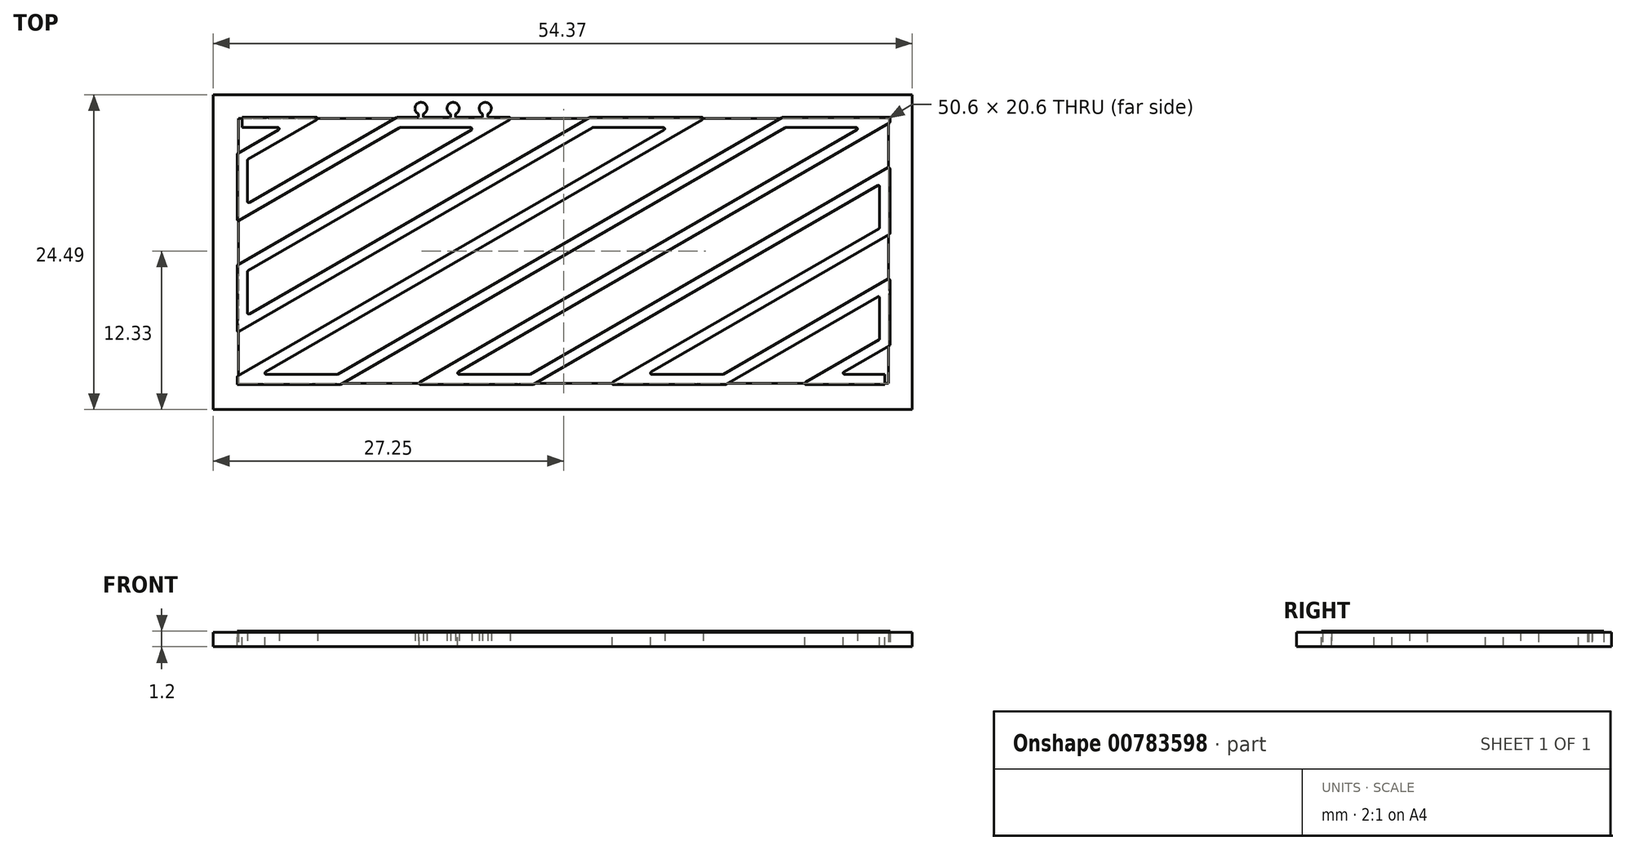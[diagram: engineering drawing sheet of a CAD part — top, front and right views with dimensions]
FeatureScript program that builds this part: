
annotation { "Feature Type Name" : "Feature", "Feature Type Description" : "" }
export const myFeature = defineFeature(function(context is Context, id is Id, definition is map)
    precondition{}
    {
        {
            var Q0;
            Q0=qCreatedBy(makeId("Top.planeOp"),FACE);
            var sketch = newSketch(context, id + "F0", { "sketchPlane" : qUnion([Q0])});
            skLineSegment(sketch, "E0.bottom", {"start": v(0, 0) * mm, "end": v(50, 0) * mm});
            skLineSegment(sketch, "E0.top", {"start": v(0, 20) * mm, "end": v(50, 20) * mm});
            skLineSegment(sketch, "E0.left", {"start": v(0, 0) * mm, "end": v(0, 20) * mm});
            skLineSegment(sketch, "E0.right", {"start": v(50, 0) * mm, "end": v(50, 20) * mm});
            skSolve(sketch);
        }
        {
            var Q0;
            Q0=qCreatedBy(makeId("Top.planeOp"),FACE);
            var sketch = newSketch(context, id + "F1", { "sketchPlane" : qUnion([Q0])});
            skLineSegment(sketch, "E1", {"start": v(0, 0) * mm, "end": v(34.64, 20) * mm});
            skLineSegment(sketch, "E2.1.0.0", {"start": v(7.5, 0) * mm, "end": v(42.14, 20) * mm});
            skLineSegment(sketch, "E2.2.0.0", {"start": v(15, 0) * mm, "end": v(49.64, 20) * mm});
            skLineSegment(sketch, "E2.3.0.0", {"start": v(22.5, 0) * mm, "end": v(50, 15.88) * mm});
            skLineSegment(sketch, "E2.4.0.0", {"start": v(30, 0) * mm, "end": v(50, 11.55) * mm});
            skLineSegment(sketch, "E2.5.0.0", {"start": v(37.5, 0) * mm, "end": v(50, 7.22) * mm});
            skLineSegment(sketch, "E2.6.0.0", {"start": v(45, 0) * mm, "end": v(50, 2.89) * mm});
            skLineSegment(sketch, "E3.1.0.0", {"start": v(0, 4.33) * mm, "end": v(27.14, 20) * mm});
            skLineSegment(sketch, "E3.2.0.0", {"start": v(0, 8.66) * mm, "end": v(19.64, 20) * mm});
            skLineSegment(sketch, "E3.3.0.0", {"start": v(0, 13) * mm, "end": v(12.14, 20) * mm});
            skLineSegment(sketch, "E3.4.0.0", {"start": v(0, 17.32) * mm, "end": v(4.64, 20) * mm});
            skLineSegment(sketch, "E4", {"start": v(0, 0) * mm, "end": v(7.5, 0) * mm});
            skLineSegment(sketch, "E5.1.0.0", {"start": v(15, 0) * mm, "end": v(22.5, 0) * mm});
            skLineSegment(sketch, "E5.2.0.0", {"start": v(30, 0) * mm, "end": v(37.5, 0) * mm});
            skLineSegment(sketch, "E5.3.0.0", {"start": v(45, 0) * mm, "end": v(50, 0) * mm});
            skLineSegment(sketch, "E6", {"start": v(0, 20) * mm, "end": v(4.64, 20) * mm});
            skLineSegment(sketch, "E7.1.0.0", {"start": v(12.14, 20) * mm, "end": v(19.64, 20) * mm});
            skLineSegment(sketch, "E7.2.0.0", {"start": v(27.14, 20) * mm, "end": v(34.64, 20) * mm});
            skLineSegment(sketch, "E7.3.0.0", {"start": v(42.14, 20) * mm, "end": v(49.64, 20) * mm});
            skPoint(sketch, "E8.orphan", {"position": v(-2.86, 20) * mm});
            skPoint(sketch, "E9.orphan", {"position": v(52.5, 0) * mm});
            skLineSegment(sketch, "E10", {"start": v(0, 4.33) * mm, "end": v(0, 8.66) * mm});
            skLineSegment(sketch, "E11", {"start": v(0, 13) * mm, "end": v(0, 17.32) * mm});
            skLineSegment(sketch, "E12", {"start": v(50, 15.88) * mm, "end": v(50, 11.55) * mm});
            skLineSegment(sketch, "E13", {"start": v(50, 7.22) * mm, "end": v(50, 2.89) * mm});
            skSolve(sketch);
        }
        {
            var Q0;
            Q0=sQuery(id+"F1.wireOp",VERTEX,"E6.start");
            var Q1;
            Q1=sQuery(id+"F1.wireOp",EDGE,"E6");
            cPlane(context, id + "F2", {"entities" : qUnion([Q0, Q1]), "cplaneType" : CPlaneType.LINE_POINT, "offset" : 25 * mm, "width" : 150 * mm, "height" : 150 * mm});
        }
        {
            var Q0;
            Q0=qCreatedBy(id+"F2.planeOp",FACE);
            var sketch = newSketch(context, id + "F3", { "sketchPlane" : qUnion([Q0])});
            skPoint(sketch, "E14.0", {"position": v(20, 0) * mm});
            skLineSegment(sketch, "E15", {"start": v(20, 0) * mm, "end": v(20.4, 0) * mm});
            skLineSegment(sketch, "E16", {"start": v(20.4, 0) * mm, "end": v(20.4, 1.2) * mm});
            skLineSegment(sketch, "E17", {"start": v(20.4, 1.2) * mm, "end": v(20, 1.2) * mm});
            skLineSegment(sketch, "E18", {"start": v(20, -0.76) * mm, "end": v(20, 2.5) * mm, "construction": true});
            skLineSegment(sketch, "E19.MirrorCS", {"start": v(19.6, 1.2) * mm, "end": v(20, 1.2) * mm});
            skLineSegment(sketch, "E20.MirrorCS", {"start": v(20, 0) * mm, "end": v(19.6, 0) * mm});
            skLineSegment(sketch, "E21.MirrorCS", {"start": v(19.6, 0) * mm, "end": v(19.6, 1.2) * mm});
            skSolve(sketch);
        }
        {
            var Q0;
            Q0=qSketchRegion(id+"F3",true);
            var Q1;
            Q1=sQuery(id+"F1.wireOp",EDGE,"E6");
            var Q2;
            Q2=sQuery(id+"F1.wireOp",EDGE,"E3.4.0.0");
            var Q3;
            Q3=sQuery(id+"F1.wireOp",EDGE,"E11");
            var Q4;
            Q4=sQuery(id+"F1.wireOp",EDGE,"E3.3.0.0");
            var Q5;
            Q5=sQuery(id+"F1.wireOp",EDGE,"E7.1.0.0");
            var Q6;
            Q6=sQuery(id+"F1.wireOp",EDGE,"E3.2.0.0");
            var Q7;
            Q7=sQuery(id+"F1.wireOp",EDGE,"E10");
            var Q8;
            Q8=sQuery(id+"F1.wireOp",EDGE,"E3.1.0.0");
            var Q9;
            Q9=sQuery(id+"F1.wireOp",EDGE,"E7.2.0.0");
            var Q10;
            Q10=sQuery(id+"F1.wireOp",EDGE,"E1");
            var Q11;
            Q11=sQuery(id+"F1.wireOp",EDGE,"E4");
            var Q12;
            Q12=sQuery(id+"F1.wireOp",EDGE,"E2.1.0.0");
            var Q13;
            Q13=sQuery(id+"F1.wireOp",EDGE,"E2.2.0.0");
            var Q14;
            Q14=sQuery(id+"F1.wireOp",EDGE,"E7.3.0.0");
            var Q15;
            Q15=sQuery(id+"F1.wireOp",EDGE,"E5.1.0.0");
            var Q16;
            Q16=sQuery(id+"F1.wireOp",EDGE,"E2.3.0.0");
            var Q17;
            Q17=sQuery(id+"F1.wireOp",EDGE,"E12");
            var Q18;
            Q18=sQuery(id+"F1.wireOp",EDGE,"E2.4.0.0");
            var Q19;
            Q19=sQuery(id+"F1.wireOp",EDGE,"E5.2.0.0");
            var Q20;
            Q20=sQuery(id+"F1.wireOp",EDGE,"E2.5.0.0");
            var Q21;
            Q21=sQuery(id+"F1.wireOp",EDGE,"E13");
            var Q22;
            Q22=sQuery(id+"F1.wireOp",EDGE,"E2.6.0.0");
            var Q23;
            Q23=sQuery(id+"F1.wireOp",EDGE,"E5.3.0.0");
            sweep(context, id + "F4", {"profiles" : qUnion([Q0]), "path" : qUnion([Q1, Q2, Q3, Q4, Q5, Q6, Q7, Q8, Q9, Q10, Q11, Q12, Q13, Q14, Q15, Q16, Q17, Q18, Q19, Q20, Q21, Q22, Q23])});
        }
        {
            var Q0;
            Q0=qCreatedBy(makeId("Top.planeOp"),FACE);
            var sketch = newSketch(context, id + "F5", { "sketchPlane" : qUnion([Q0])});
            skLineSegment(sketch, "E22.0", {"start": v(-0.4, 8.9) * mm, "end": v(-0.4, 3.64) * mm});
            skLineSegment(sketch, "E23.0", {"start": v(0, 20.4) * mm, "end": v(6.13, 20.4) * mm});
            skLineSegment(sketch, "E24.0", {"start": v(28.5, -0.4) * mm, "end": v(37.6, -0.4) * mm});
            skLineSegment(sketch, "E25.0", {"start": v(50.4, 16.57) * mm, "end": v(50.4, 11.32) * mm});
            skLineSegment(sketch, "E26.bottom", {"start": v(-0.4, 20.4) * mm, "end": v(50.4, 20.4) * mm});
            skLineSegment(sketch, "E26.top", {"start": v(-0.4, -0.4) * mm, "end": v(50.4, -0.4) * mm});
            skLineSegment(sketch, "E26.left", {"start": v(-0.4, 20.4) * mm, "end": v(-0.4, -0.4) * mm});
            skLineSegment(sketch, "E26.right", {"start": v(50.4, 20.4) * mm, "end": v(50.4, -0.4) * mm});
            skLineSegment(sketch, "E27.bottom", {"start": v(-6.4, 28.18) * mm, "end": v(56.43, 28.18) * mm});
            skLineSegment(sketch, "E27.top", {"start": v(-6.4, -9.1) * mm, "end": v(56.43, -9.1) * mm});
            skLineSegment(sketch, "E27.left", {"start": v(-6.4, 28.18) * mm, "end": v(-6.4, -9.1) * mm});
            skLineSegment(sketch, "E27.right", {"start": v(56.43, 28.18) * mm, "end": v(56.43, -9.1) * mm});
            skSolve(sketch);
        }
        {
            var Q0;
            {var subQ1=sQuery(id+"F5.wireOp",EDGE,"E22.0");Q0=makeQuery(id+"F5.imprint","IMPRINT",FACE,{"disambiguationData":[TD([[makeQuery(id+"F5.imprint","IMPRINT",EDGE,{"derivedFrom":subQ1}),-1.0]])]});}
            extrude(context, id + "F6", {"entities" : qUnion([Q0]), "depth" : 25 * mm, "offsetDistance" : 25 * mm});
        }
        {
            var Q0;
            Q0=makeQuery(id+"F6.opExtrude","SWEPT_BODY",BODY,{"disambiguationData":[OSD([sQuery(id+"F5.wireOp",EDGE,"E22.0"),sQuery(id+"F5.wireOp",EDGE,"E23.0"),sQuery(id+"F5.wireOp",EDGE,"E24.0"),sQuery(id+"F5.wireOp",EDGE,"E25.0"),sQuery(id+"F5.wireOp",EDGE,"E26.bottom"),sQuery(id+"F5.wireOp",EDGE,"E26.top"),sQuery(id+"F5.wireOp",EDGE,"E26.left"),sQuery(id+"F5.wireOp",EDGE,"E26.right"),sQuery(id+"F5.wireOp",EDGE,"E27.bottom"),sQuery(id+"F5.wireOp",EDGE,"E27.top"),sQuery(id+"F5.wireOp",EDGE,"E27.left"),sQuery(id+"F5.wireOp",EDGE,"E27.right")])]});
            var Q1;
            Q1=makeQuery(id+"F4.opSweep","SWEPT_BODY",BODY,{"disambiguationData":[OSD([sQuery(id+"F1.wireOp",EDGE,"E2.1.0.0"),sQuery(id+"F3.wireOp",EDGE,"E15"),sQuery(id+"F3.wireOp",EDGE,"E16"),sQuery(id+"F3.wireOp",EDGE,"E17"),sQuery(id+"F3.wireOp",EDGE,"E19.MirrorCS"),sQuery(id+"F3.wireOp",EDGE,"E20.MirrorCS"),sQuery(id+"F3.wireOp",EDGE,"E21.MirrorCS")])]});
            booleanBodies(context, id + "F7", {"operationType" : BooleanOperationType.SUBTRACTION, "tools" : qUnion([Q0]), "targets" : qUnion([Q1])});
        }
        {
            var Q0;
            Q0=qCreatedBy(makeId("Top.planeOp"),FACE);
            var sketch = newSketch(context, id + "F8", { "sketchPlane" : qUnion([Q0])});
            skLineSegment(sketch, "E28.0", {"start": v(-0.3, 20.3) * mm, "end": v(50.3, 20.3) * mm});
            skLineSegment(sketch, "E28.1", {"start": v(-0.3, 20.3) * mm, "end": v(-0.3, -0.3) * mm});
            skLineSegment(sketch, "E28.2", {"start": v(-0.3, -0.3) * mm, "end": v(50.3, -0.3) * mm});
            skLineSegment(sketch, "E28.3", {"start": v(50.3, 20.3) * mm, "end": v(50.3, -0.3) * mm});
            skSolve(sketch);
        }
        {
            var Q0;
            Q0=qSketchRegion(id+"F8",true);
            extrude(context, id + "F9", {"entities" : qUnion([Q0]), "depth" : 1.1 * mm, "offsetDistance" : 25 * mm});
        }
        {
            var Q0;
            Q0=makeQuery(id+"F4.opSweep","MID_CAP_EDGE",EDGE,{"disambiguationData":[OSD([sQuery(id+"F1.wireOp",VERTEX,"E11.end"),sQuery(id+"F3.wireOp",EDGE,"E21.MirrorCS")])],"capPos":2.0});
            var Q1;
            Q1=makeQuery(id+"F4.opSweep","MID_CAP_EDGE",EDGE,{"disambiguationData":[OSD([sQuery(id+"F1.wireOp",VERTEX,"E3.4.0.0.end"),sQuery(id+"F3.wireOp",EDGE,"E21.MirrorCS")])],"capPos":1.0});
            var Q2;
            Q2=makeQuery(id+"F4.opSweep","MID_CAP_EDGE",EDGE,{"disambiguationData":[OSD([sQuery(id+"F1.wireOp",VERTEX,"E3.4.0.0.end"),sQuery(id+"F3.wireOp",EDGE,"E16")])],"capPos":1.0});
            var Q3;
            Q3=makeQuery(id+"F4.opSweep","MID_CAP_EDGE",EDGE,{"disambiguationData":[OSD([sQuery(id+"F1.wireOp",VERTEX,"E11.end"),sQuery(id+"F3.wireOp",EDGE,"E16")])],"capPos":2.0});
            var Q4;
            Q4=makeQuery(id+"F4.opSweep","MID_CAP_EDGE",EDGE,{"disambiguationData":[OSD([sQuery(id+"F1.wireOp",VERTEX,"E3.3.0.0.start"),sQuery(id+"F3.wireOp",EDGE,"E16")])],"capPos":3.0});
            var Q5;
            Q5=makeQuery(id+"F4.opSweep","MID_CAP_EDGE",EDGE,{"disambiguationData":[OSD([sQuery(id+"F1.wireOp",VERTEX,"E3.3.0.0.start"),sQuery(id+"F3.wireOp",EDGE,"E21.MirrorCS")])],"capPos":3.0});
            var Q6;
            Q6=makeQuery(id+"F4.opSweep","MID_CAP_EDGE",EDGE,{"disambiguationData":[OSD([sQuery(id+"F1.wireOp",VERTEX,"E7.1.0.0.start"),sQuery(id+"F3.wireOp",EDGE,"E21.MirrorCS")])],"capPos":4.0});
            var Q7;
            Q7=makeQuery(id+"F4.opSweep","MID_CAP_EDGE",EDGE,{"disambiguationData":[OSD([sQuery(id+"F1.wireOp",VERTEX,"E7.1.0.0.start"),sQuery(id+"F3.wireOp",EDGE,"E16")])],"capPos":4.0});
            var Q8;
            Q8=makeQuery(id+"F4.opSweep","MID_CAP_EDGE",EDGE,{"disambiguationData":[OSD([sQuery(id+"F1.wireOp",VERTEX,"E3.2.0.0.end"),sQuery(id+"F3.wireOp",EDGE,"E21.MirrorCS")])],"capPos":5.0});
            var Q9;
            Q9=makeQuery(id+"F4.opSweep","MID_CAP_EDGE",EDGE,{"disambiguationData":[OSD([sQuery(id+"F1.wireOp",VERTEX,"E3.2.0.0.end"),sQuery(id+"F3.wireOp",EDGE,"E16")])],"capPos":5.0});
            var Q10;
            Q10=makeQuery(id+"F4.opSweep","MID_CAP_EDGE",EDGE,{"disambiguationData":[OSD([sQuery(id+"F1.wireOp",VERTEX,"E7.2.0.0.start"),sQuery(id+"F3.wireOp",EDGE,"E16")])],"capPos":8.0});
            var Q11;
            Q11=makeQuery(id+"F4.opSweep","MID_CAP_EDGE",EDGE,{"disambiguationData":[OSD([sQuery(id+"F1.wireOp",VERTEX,"E10.end"),sQuery(id+"F3.wireOp",EDGE,"E21.MirrorCS")])],"capPos":6.0});
            var Q12;
            Q12=makeQuery(id+"F4.opSweep","MID_CAP_EDGE",EDGE,{"disambiguationData":[OSD([sQuery(id+"F1.wireOp",VERTEX,"E10.end"),sQuery(id+"F3.wireOp",EDGE,"E16")])],"capPos":6.0});
            var Q13;
            Q13=makeQuery(id+"F4.opSweep","MID_CAP_EDGE",EDGE,{"disambiguationData":[OSD([sQuery(id+"F1.wireOp",VERTEX,"E3.1.0.0.start"),sQuery(id+"F3.wireOp",EDGE,"E16")])],"capPos":7.0});
            var Q14;
            Q14=makeQuery(id+"F4.opSweep","MID_CAP_EDGE",EDGE,{"disambiguationData":[OSD([sQuery(id+"F1.wireOp",VERTEX,"E3.1.0.0.start"),sQuery(id+"F3.wireOp",EDGE,"E21.MirrorCS")])],"capPos":7.0});
            var Q15;
            Q15=makeQuery(id+"F4.opSweep","MID_CAP_EDGE",EDGE,{"disambiguationData":[OSD([sQuery(id+"F1.wireOp",VERTEX,"E7.2.0.0.start"),sQuery(id+"F3.wireOp",EDGE,"E21.MirrorCS")])],"capPos":8.0});
            var Q16;
            Q16=makeQuery(id+"F4.opSweep","MID_CAP_EDGE",EDGE,{"disambiguationData":[OSD([sQuery(id+"F1.wireOp",VERTEX,"E1.end"),sQuery(id+"F3.wireOp",EDGE,"E21.MirrorCS")])],"capPos":9.0});
            var Q17;
            Q17=makeQuery(id+"F4.opSweep","MID_CAP_EDGE",EDGE,{"disambiguationData":[OSD([sQuery(id+"F1.wireOp",VERTEX,"E1.end"),sQuery(id+"F3.wireOp",EDGE,"E16")])],"capPos":9.0});
            var Q18;
            Q18=makeQuery(id+"F4.opSweep","MID_CAP_EDGE",EDGE,{"disambiguationData":[OSD([sQuery(id+"F1.wireOp",VERTEX,"E7.3.0.0.start"),sQuery(id+"F3.wireOp",EDGE,"E16")])],"capPos":12.0});
            var Q19;
            Q19=makeQuery(id+"F7.opBoolean","INTERSECT",EDGE,{"derivedFrom":[makeQuery(id+"F4.opSweep","SWEPT_FACE",FACE,{"disambiguationData":[OSD([sQuery(id+"F1.wireOp",EDGE,"E1"),sQuery(id+"F3.wireOp",EDGE,"E21.MirrorCS")])]}),makeQuery(id+"F6.opExtrude","SWEPT_FACE",FACE,{"disambiguationData":[OSD([sQuery(id+"F5.wireOp",EDGE,"E22.0"),sQuery(id+"F5.wireOp",EDGE,"E26.left")])]})]});
            var Q20;
            Q20=makeQuery(id+"F4.opSweep","MID_CAP_EDGE",EDGE,{"disambiguationData":[OSD([sQuery(id+"F1.wireOp",VERTEX,"E4.start"),sQuery(id+"F3.wireOp",EDGE,"E16")])],"capPos":10.0});
            var Q21;
            Q21=makeQuery(id+"F7.opBoolean","COPY",EDGE,{"derivedFrom":makeQuery(id+"F6.opExtrude","SWEPT_EDGE",EDGE,{"disambiguationData":[OSD([sQuery(id+"F5.wireOp",EDGE,"E26.top"),sQuery(id+"F5.wireOp",EDGE,"E26.left")])]})});
            var Q22;
            Q22=makeQuery(id+"F4.opSweep","MID_CAP_EDGE",EDGE,{"disambiguationData":[OSD([sQuery(id+"F1.wireOp",VERTEX,"E2.1.0.0.start"),sQuery(id+"F3.wireOp",EDGE,"E16")])],"capPos":11.0});
            var Q23;
            Q23=makeQuery(id+"F4.opSweep","MID_CAP_EDGE",EDGE,{"disambiguationData":[OSD([sQuery(id+"F1.wireOp",VERTEX,"E2.1.0.0.start"),sQuery(id+"F3.wireOp",EDGE,"E21.MirrorCS")])],"capPos":11.0});
            var Q24;
            Q24=makeQuery(id+"F4.opSweep","MID_CAP_EDGE",EDGE,{"disambiguationData":[OSD([sQuery(id+"F1.wireOp",VERTEX,"E7.3.0.0.start"),sQuery(id+"F3.wireOp",EDGE,"E21.MirrorCS")])],"capPos":12.0});
            var Q25;
            Q25=makeQuery(id+"F4.opSweep","MID_CAP_EDGE",EDGE,{"disambiguationData":[OSD([sQuery(id+"F1.wireOp",VERTEX,"E7.3.0.0.end"),sQuery(id+"F3.wireOp",EDGE,"E21.MirrorCS")])],"capPos":13.0});
            var Q26;
            Q26=makeQuery(id+"F7.opBoolean","COPY",EDGE,{"derivedFrom":makeQuery(id+"F6.opExtrude","SWEPT_EDGE",EDGE,{"disambiguationData":[OSD([sQuery(id+"F5.wireOp",EDGE,"E26.bottom"),sQuery(id+"F5.wireOp",EDGE,"E26.right")])]})});
            var Q27;
            Q27=makeQuery(id+"F7.opBoolean","INTERSECT",EDGE,{"derivedFrom":[makeQuery(id+"F4.opSweep","SWEPT_FACE",FACE,{"disambiguationData":[OSD([sQuery(id+"F1.wireOp",EDGE,"E2.2.0.0"),sQuery(id+"F3.wireOp",EDGE,"E16")])]}),makeQuery(id+"F6.opExtrude","SWEPT_FACE",FACE,{"disambiguationData":[OSD([sQuery(id+"F5.wireOp",EDGE,"E25.0"),sQuery(id+"F5.wireOp",EDGE,"E26.right")])]})]});
            var Q28;
            Q28=makeQuery(id+"F4.opSweep","MID_CAP_EDGE",EDGE,{"disambiguationData":[OSD([sQuery(id+"F1.wireOp",VERTEX,"E12.start"),sQuery(id+"F3.wireOp",EDGE,"E16")])],"capPos":16.0});
            var Q29;
            Q29=makeQuery(id+"F4.opSweep","MID_CAP_EDGE",EDGE,{"disambiguationData":[OSD([sQuery(id+"F1.wireOp",VERTEX,"E12.start"),sQuery(id+"F3.wireOp",EDGE,"E21.MirrorCS")])],"capPos":16.0});
            var Q30;
            Q30=makeQuery(id+"F4.opSweep","MID_CAP_EDGE",EDGE,{"disambiguationData":[OSD([sQuery(id+"F1.wireOp",VERTEX,"E2.4.0.0.end"),sQuery(id+"F3.wireOp",EDGE,"E21.MirrorCS")])],"capPos":17.0});
            var Q31;
            Q31=makeQuery(id+"F4.opSweep","MID_CAP_EDGE",EDGE,{"disambiguationData":[OSD([sQuery(id+"F1.wireOp",VERTEX,"E2.4.0.0.end"),sQuery(id+"F3.wireOp",EDGE,"E16")])],"capPos":17.0});
            var Q32;
            Q32=makeQuery(id+"F4.opSweep","MID_CAP_EDGE",EDGE,{"disambiguationData":[OSD([sQuery(id+"F1.wireOp",VERTEX,"E5.2.0.0.start"),sQuery(id+"F3.wireOp",EDGE,"E21.MirrorCS")])],"capPos":18.0});
            var Q33;
            Q33=makeQuery(id+"F4.opSweep","MID_CAP_EDGE",EDGE,{"disambiguationData":[OSD([sQuery(id+"F1.wireOp",VERTEX,"E5.2.0.0.start"),sQuery(id+"F3.wireOp",EDGE,"E16")])],"capPos":18.0});
            var Q34;
            Q34=makeQuery(id+"F4.opSweep","MID_CAP_EDGE",EDGE,{"disambiguationData":[OSD([sQuery(id+"F1.wireOp",VERTEX,"E2.3.0.0.start"),sQuery(id+"F3.wireOp",EDGE,"E21.MirrorCS")])],"capPos":15.0});
            var Q35;
            Q35=makeQuery(id+"F4.opSweep","MID_CAP_EDGE",EDGE,{"disambiguationData":[OSD([sQuery(id+"F1.wireOp",VERTEX,"E5.1.0.0.start"),sQuery(id+"F3.wireOp",EDGE,"E21.MirrorCS")])],"capPos":14.0});
            var Q36;
            Q36=makeQuery(id+"F4.opSweep","MID_CAP_EDGE",EDGE,{"disambiguationData":[OSD([sQuery(id+"F1.wireOp",VERTEX,"E5.1.0.0.start"),sQuery(id+"F3.wireOp",EDGE,"E16")])],"capPos":14.0});
            var Q37;
            Q37=makeQuery(id+"F4.opSweep","MID_CAP_EDGE",EDGE,{"disambiguationData":[OSD([sQuery(id+"F1.wireOp",VERTEX,"E2.5.0.0.start"),sQuery(id+"F3.wireOp",EDGE,"E16")])],"capPos":19.0});
            var Q38;
            Q38=makeQuery(id+"F4.opSweep","MID_CAP_EDGE",EDGE,{"disambiguationData":[OSD([sQuery(id+"F1.wireOp",VERTEX,"E2.3.0.0.start"),sQuery(id+"F3.wireOp",EDGE,"E16")])],"capPos":15.0});
            var Q39;
            Q39=makeQuery(id+"F4.opSweep","MID_CAP_EDGE",EDGE,{"disambiguationData":[OSD([sQuery(id+"F1.wireOp",VERTEX,"E13.start"),sQuery(id+"F3.wireOp",EDGE,"E16")])],"capPos":20.0});
            var Q40;
            Q40=makeQuery(id+"F4.opSweep","MID_CAP_EDGE",EDGE,{"disambiguationData":[OSD([sQuery(id+"F1.wireOp",VERTEX,"E13.start"),sQuery(id+"F3.wireOp",EDGE,"E21.MirrorCS")])],"capPos":20.0});
            var Q41;
            Q41=makeQuery(id+"F4.opSweep","MID_CAP_EDGE",EDGE,{"disambiguationData":[OSD([sQuery(id+"F1.wireOp",VERTEX,"E2.5.0.0.start"),sQuery(id+"F3.wireOp",EDGE,"E21.MirrorCS")])],"capPos":19.0});
            var Q42;
            Q42=makeQuery(id+"F4.opSweep","MID_CAP_EDGE",EDGE,{"disambiguationData":[OSD([sQuery(id+"F1.wireOp",VERTEX,"E5.3.0.0.start"),sQuery(id+"F3.wireOp",EDGE,"E21.MirrorCS")])],"capPos":22.0});
            var Q43;
            Q43=makeQuery(id+"F4.opSweep","MID_CAP_EDGE",EDGE,{"disambiguationData":[OSD([sQuery(id+"F1.wireOp",VERTEX,"E2.6.0.0.end"),sQuery(id+"F3.wireOp",EDGE,"E16")])],"capPos":21.0});
            var Q44;
            Q44=makeQuery(id+"F4.opSweep","MID_CAP_EDGE",EDGE,{"disambiguationData":[OSD([sQuery(id+"F1.wireOp",VERTEX,"E5.3.0.0.start"),sQuery(id+"F3.wireOp",EDGE,"E16")])],"capPos":22.0});
            var Q45;
            Q45=makeQuery(id+"F4.opSweep","MID_CAP_EDGE",EDGE,{"disambiguationData":[OSD([sQuery(id+"F1.wireOp",VERTEX,"E2.6.0.0.end"),sQuery(id+"F3.wireOp",EDGE,"E21.MirrorCS")])],"capPos":21.0});
            fillet(context, id + "F10", {"entities" : qUnion([Q0, Q1, Q2, Q3, Q4, Q5, Q6, Q7, Q8, Q9, Q10, Q11, Q12, Q13, Q14, Q15, Q16, Q17, Q18, Q19, Q20, Q21, Q22, Q23, Q24, Q25, Q26, Q27, Q28, Q29, Q30, Q31, Q32, Q33, Q34, Q35, Q36, Q37, Q38, Q39, Q40, Q41, Q42, Q43, Q44, Q45]), "radius" : .1 * mm, "tangentPropagation" : true, "allowEdgeOverflow" : false});
        }
        {
            var Q0;
            Q0=qCreatedBy(makeId("Top.planeOp"),FACE);
            var sketch = newSketch(context, id + "F11", { "sketchPlane" : qUnion([Q0])});
            skArc(sketch, "E29", {"start": v(16.6, 20.66) * mm, "mid": v(16.42, 21.56) * mm, "end": v(16.2, 20.67) * mm});
            skPoint(sketch, "E29.centerSnap0", {"position": v(16.41, 20.4) * mm});
            skLineSegment(sketch, "E30", {"start": v(16.2, 20.67) * mm, "end": v(16.2, 20.4) * mm});
            skLineSegment(sketch, "E31", {"start": v(16.6, 20.66) * mm, "end": v(16.6, 20.4) * mm});
            skArc(sketch, "E32.1.0.0", {"start": v(19.1, 20.66) * mm, "mid": v(18.92, 21.56) * mm, "end": v(18.7, 20.67) * mm});
            skPoint(sketch, "E32.1.0.1", {"position": v(18.91, 20.4) * mm});
            skLineSegment(sketch, "E32.1.0.2", {"start": v(19.1, 20.66) * mm, "end": v(19.1, 20.4) * mm});
            skLineSegment(sketch, "E32.1.0.3", {"start": v(18.7, 20.67) * mm, "end": v(18.7, 20.4) * mm});
            skPoint(sketch, "E33.1.0.0", {"position": v(13.91, 20.4) * mm});
            skArc(sketch, "E33.1.0.1", {"start": v(14.1, 20.66) * mm, "mid": v(13.92, 21.56) * mm, "end": v(13.7, 20.67) * mm});
            skLineSegment(sketch, "E33.1.0.2", {"start": v(13.7, 20.67) * mm, "end": v(13.7, 20.4) * mm});
            skLineSegment(sketch, "E33.1.0.3", {"start": v(14.1, 20.66) * mm, "end": v(14.1, 20.4) * mm});
            skLineSegment(sketch, "E33.direction1", {"start": v(16.2, 20.4) * mm, "end": v(13.7, 20.4) * mm, "construction": true});
            skLineSegment(sketch, "E34", {"start": v(18.7, 20.4) * mm, "end": v(19.1, 20.4) * mm});
            skLineSegment(sketch, "E35", {"start": v(16.2, 20.4) * mm, "end": v(16.6, 20.4) * mm});
            skLineSegment(sketch, "E36", {"start": v(13.7, 20.4) * mm, "end": v(14.1, 20.4) * mm});
            skSolve(sketch);
        }
        {
            var Q0;
            Q0 = qSketchRegion(id + "F11", true);
            var Q1;
            Q1=makeQuery(id+"F4.opSweep","SWEPT_FACE",FACE,{"disambiguationData":[OSD([sQuery(id+"F1.wireOp",EDGE,"E6"),sQuery(id+"F3.wireOp",EDGE,"E17"),sQuery(id+"F3.wireOp",EDGE,"E19.MirrorCS")])]});
            extrude(context, id + "F12", {"entities" : qUnion([Q0]), "operationType" : NewBodyOperationType.ADD, "endBound" : BoundingType.UP_TO_SURFACE, "depth" : 25 * mm, "endBoundEntityFace" : qUnion([Q1]), "offsetDistance" : 25 * mm});
        }
        {
            var Q0;
            Q0=qCreatedBy(makeId("Top.planeOp"),FACE);
            var sketch = newSketch(context, id + "F13", { "sketchPlane" : qUnion([Q0])});
            skPoint(sketch, "E37.0", {"position": v(-0.3, 20.3) * mm});
            skPoint(sketch, "E38.0", {"position": v(50.3, -0.3) * mm});
            skLineSegment(sketch, "E39.bottom", {"start": v(-0.3, 20.3) * mm, "end": v(50.3, 20.3) * mm});
            skLineSegment(sketch, "E39.top", {"start": v(-0.3, -0.3) * mm, "end": v(50.3, -0.3) * mm});
            skLineSegment(sketch, "E39.left", {"start": v(-0.3, 20.3) * mm, "end": v(-0.3, -0.3) * mm});
            skLineSegment(sketch, "E39.right", {"start": v(50.3, 20.3) * mm, "end": v(50.3, -0.3) * mm});
            skLineSegment(sketch, "E40.bottom", {"start": v(52.12, -2.33) * mm, "end": v(-2.25, -2.33) * mm});
            skLineSegment(sketch, "E40.top", {"start": v(52.12, 22.16) * mm, "end": v(-2.25, 22.16) * mm});
            skLineSegment(sketch, "E40.left", {"start": v(52.12, -2.33) * mm, "end": v(52.12, 22.16) * mm});
            skLineSegment(sketch, "E40.right", {"start": v(-2.25, -2.33) * mm, "end": v(-2.25, 22.16) * mm});
            skSolve(sketch);
        }
        {
            var Q0;
            Q0 = qSketchRegion(id + "F13", true);
            var Q1;
            Q1=makeQuery(id+"F9.opExtrude","CAP_FACE",FACE,{"disambiguationData":[OSD([sQuery(id+"F8.wireOp",EDGE,"E28.0"),sQuery(id+"F8.wireOp",EDGE,"E28.1"),sQuery(id+"F8.wireOp",EDGE,"E28.2"),sQuery(id+"F8.wireOp",EDGE,"E28.3")])],"isStart":false});
            extrude(context, id + "F14", {"entities" : qUnion([Q0]), "endBound" : BoundingType.UP_TO_SURFACE, "depth" : 25 * mm, "endBoundEntityFace" : qUnion([Q1]), "offsetDistance" : 25 * mm});
        }
    });
